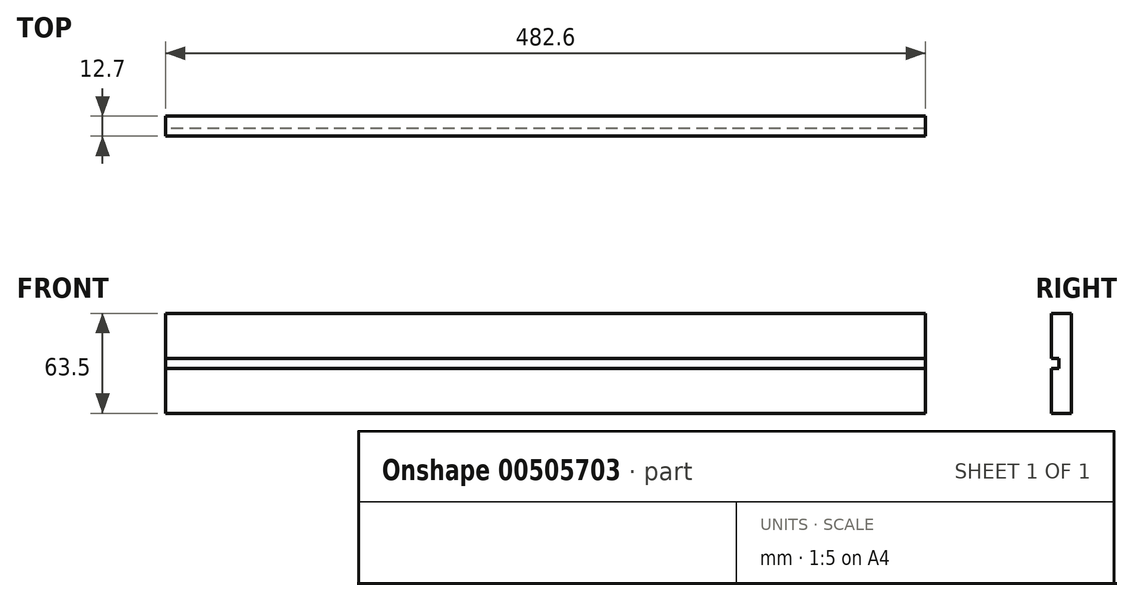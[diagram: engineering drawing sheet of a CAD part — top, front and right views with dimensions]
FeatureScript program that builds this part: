
annotation { "Feature Type Name" : "Feature", "Feature Type Description" : "" }
export const myFeature = defineFeature(function(context is Context, id is Id, definition is map)
    precondition{}
    {
        {
            var Q0;
            Q0=qCreatedBy(makeId("Right.planeOp"),FACE);
            var sketch = newSketch(context, id + "F0", { "sketchPlane" : qUnion([Q0])});
            skLineSegment(sketch, "E0.bottom", {"start": v(0, 31.75) * mm, "end": v(12.7, 31.75) * mm});
            skLineSegment(sketch, "E0.top", {"start": v(0, -31.75) * mm, "end": v(12.7, -31.75) * mm});
            skLineSegment(sketch, "E0.left", {"start": v(0, 31.75) * mm, "end": v(0, 3.18) * mm});
            skLineSegment(sketch, "E0.right", {"start": v(12.7, 31.75) * mm, "end": v(12.7, -31.75) * mm});
            skLineSegment(sketch, "E1", {"start": v(0, 3.18) * mm, "end": v(4.76, 3.18) * mm});
            skLineSegment(sketch, "E2.MirrorCS", {"start": v(0, -3.18) * mm, "end": v(4.76, -3.18) * mm});
            skLineSegment(sketch, "E3", {"start": v(4.76, -3.18) * mm, "end": v(4.76, 3.18) * mm});
            skLineSegment(sketch, "E4.trimOffspring", {"start": v(0, -3.17) * mm, "end": v(0, -31.75) * mm});
            skSolve(sketch);
        }
        {
            var Q0;
            Q0 = qSketchRegion(id + "F0", true);
            extrude(context, id + "F1", {"entities" : qUnion([Q0]), "endBound" : BoundingType.SYMMETRIC, "depth" : 482.6 * mm});
        }
    });
